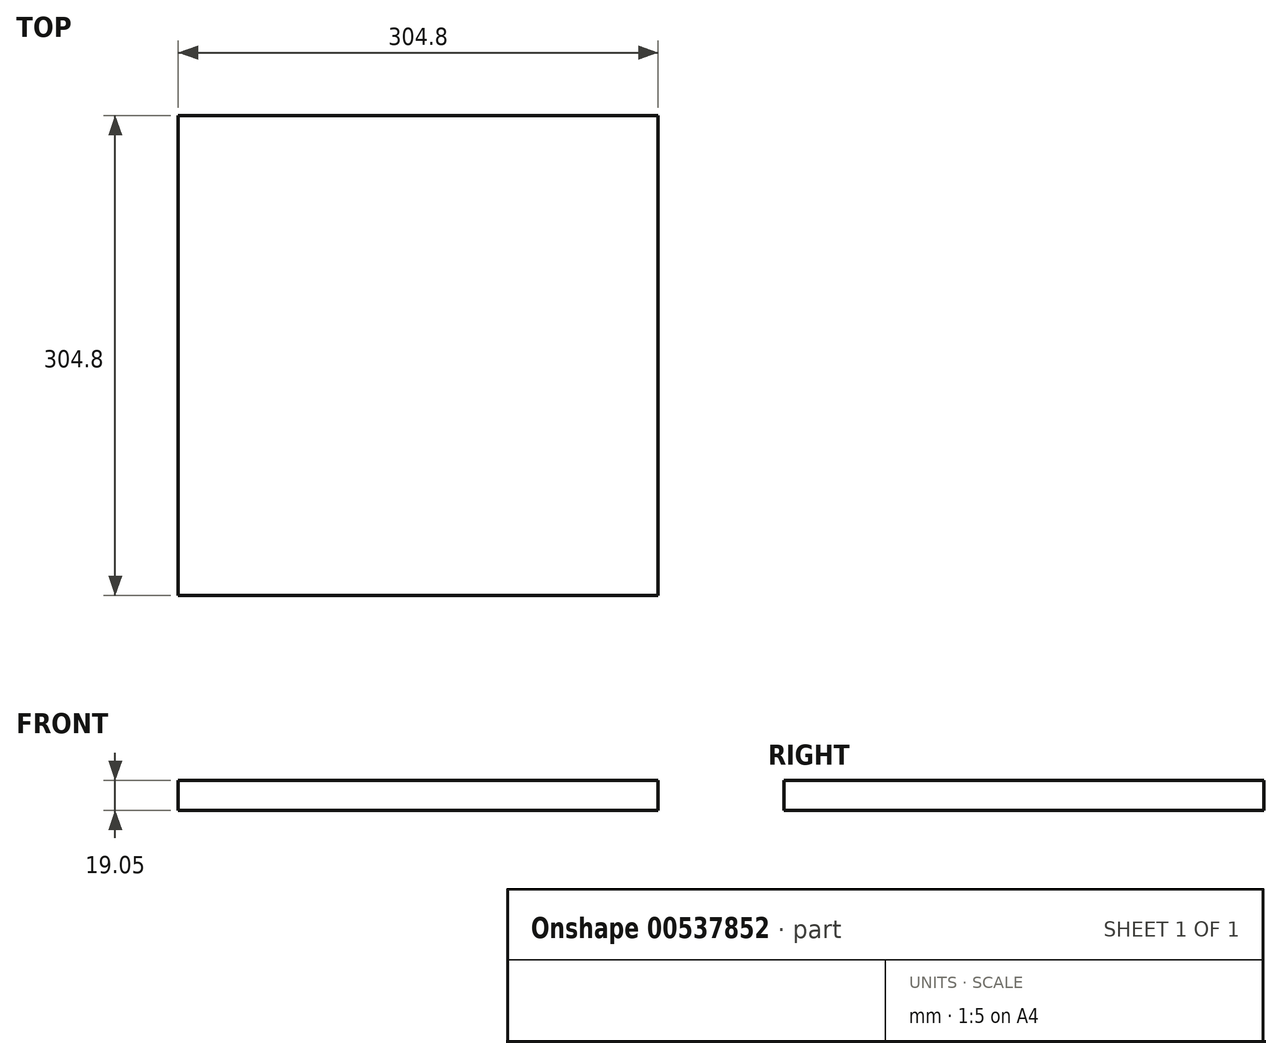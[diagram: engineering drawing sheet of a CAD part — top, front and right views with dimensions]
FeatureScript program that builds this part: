
annotation { "Feature Type Name" : "Feature", "Feature Type Description" : "" }
export const myFeature = defineFeature(function(context is Context, id is Id, definition is map)
    precondition{}
    {
        {
            var Q0;
            Q0=qCreatedBy(makeId("Top.planeOp"),FACE);
            var sketch = newSketch(context, id + "F0", { "sketchPlane" : qUnion([Q0])});
            skLineSegment(sketch, "E0.bottom", {"start": v(152.4, -152.4) * mm, "end": v(-152.4, -152.4) * mm});
            skLineSegment(sketch, "E0.top", {"start": v(152.4, 152.4) * mm, "end": v(-152.4, 152.4) * mm});
            skLineSegment(sketch, "E0.left", {"start": v(152.4, -152.4) * mm, "end": v(152.4, 152.4) * mm});
            skLineSegment(sketch, "E0.right", {"start": v(-152.4, -152.4) * mm, "end": v(-152.4, 152.4) * mm});
            skPoint(sketch, "E0.middle", {"position": v(0, 0) * mm});
            skSolve(sketch);
        }
        {
            var Q0;
            Q0 = qSketchRegion(id + "F0", true);
            extrude(context, id + "F1", {"entities" : qUnion([Q0]), "depth" : 19.05 * mm, "offsetDistance" : 25.4 * mm});
        }
    });
